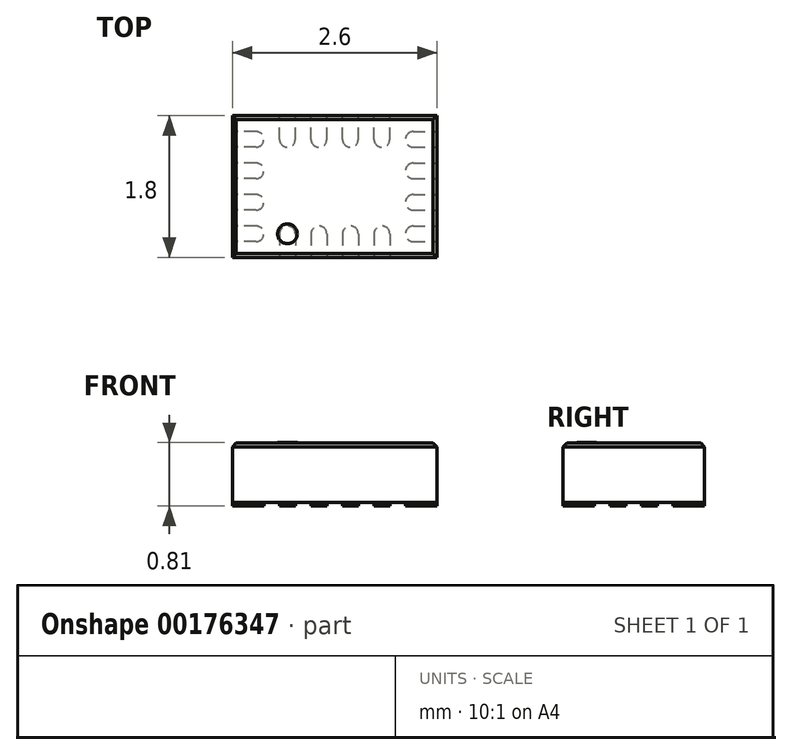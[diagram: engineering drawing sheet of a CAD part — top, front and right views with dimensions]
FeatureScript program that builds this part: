
annotation { "Feature Type Name" : "Feature", "Feature Type Description" : "" }
export const myFeature = defineFeature(function(context is Context, id is Id, definition is map)
    precondition{}
    {
        {
            var Q0;
            Q0=qCreatedBy(makeId("Top.planeOp"),FACE);
            var sketch = newSketch(context, id + "F0", { "sketchPlane" : qUnion([Q0])});
            skLineSegment(sketch, "E0.bottom", {"start": v(1.3, -0.9) * mm, "end": v(-1.3, -0.9) * mm});
            skLineSegment(sketch, "E0.top", {"start": v(1.3, 0.9) * mm, "end": v(-1.3, 0.9) * mm});
            skLineSegment(sketch, "E0.left", {"start": v(1.3, -0.9) * mm, "end": v(1.3, 0.9) * mm});
            skLineSegment(sketch, "E0.right", {"start": v(-1.3, -0.9) * mm, "end": v(-1.3, 0.9) * mm});
            skPoint(sketch, "E0.middle", {"position": v(0, 0) * mm});
            skSolve(sketch);
        }
        {
            var Q0;
            Q0=makeQuery(id+"F0.imprint","IMPRINT",FACE,{"disambiguationData":[TD([[makeQuery(id+"F0.imprint","IMPRINT",EDGE,{"derivedFrom":sQuery(id+"F0.wireOp",EDGE,"E0.bottom")}),-1.0]])]});
            extrude(context, id + "F1", {"entities" : qUnion([Q0]), "depth" : 0.75 * mm});
        }
        {
            var Q0;
            Q0=qCreatedBy(makeId("Top.planeOp"),FACE);
            var sketch = newSketch(context, id + "F2", { "sketchPlane" : qUnion([Q0])});
            skArc(sketch, "E1", {"start": v(-0.5, -0.6) * mm, "mid": v(-0.6, -0.5) * mm, "end": v(-0.7, -0.6) * mm});
            skLineSegment(sketch, "E2", {"start": v(-0.7, -0.6) * mm, "end": v(-0.6, -0.6) * mm, "construction": true});
            skLineSegment(sketch, "E3", {"start": v(-0.5, -0.6) * mm, "end": v(-0.6, -0.6) * mm, "construction": true});
            skLineSegment(sketch, "E4", {"start": v(-0.7, -0.6) * mm, "end": v(-0.7, -0.9) * mm});
            skLineSegment(sketch, "E5", {"start": v(-0.5, -0.6) * mm, "end": v(-0.5, -0.9) * mm});
            skLineSegment(sketch, "E6", {"start": v(-0.5, -0.9) * mm, "end": v(-0.7, -0.9) * mm});
            skLineSegment(sketch, "E7", {"start": v(-0.6, -0.9) * mm, "end": v(-0.6, -0.5) * mm, "construction": true});
            skArc(sketch, "E8.1.0.0", {"start": v(-0.1, -0.6) * mm, "mid": v(-0.2, -0.5) * mm, "end": v(-0.3, -0.6) * mm});
            skLineSegment(sketch, "E8.1.0.1", {"start": v(-0.1, -0.6) * mm, "end": v(-0.1, -0.9) * mm});
            skLineSegment(sketch, "E8.1.0.2", {"start": v(-0.2, -0.9) * mm, "end": v(-0.2, -0.5) * mm, "construction": true});
            skLineSegment(sketch, "E8.1.0.3", {"start": v(-0.3, -0.6) * mm, "end": v(-0.3, -0.9) * mm});
            skLineSegment(sketch, "E8.1.0.4", {"start": v(-0.1, -0.9) * mm, "end": v(-0.3, -0.9) * mm});
            skLineSegment(sketch, "E8.1.0.5", {"start": v(-0.3, -0.6) * mm, "end": v(-0.2, -0.6) * mm, "construction": true});
            skLineSegment(sketch, "E8.1.0.6", {"start": v(-0.1, -0.6) * mm, "end": v(-0.2, -0.6) * mm, "construction": true});
            skArc(sketch, "E8.2.0.0", {"start": v(0.3, -0.6) * mm, "mid": v(0.2, -0.5) * mm, "end": v(0.1, -0.6) * mm});
            skLineSegment(sketch, "E8.2.0.1", {"start": v(0.3, -0.6) * mm, "end": v(0.3, -0.9) * mm});
            skLineSegment(sketch, "E8.2.0.2", {"start": v(0.2, -0.9) * mm, "end": v(0.2, -0.5) * mm, "construction": true});
            skLineSegment(sketch, "E8.2.0.3", {"start": v(0.1, -0.6) * mm, "end": v(0.1, -0.9) * mm});
            skLineSegment(sketch, "E8.2.0.4", {"start": v(0.3, -0.9) * mm, "end": v(0.1, -0.9) * mm});
            skLineSegment(sketch, "E8.2.0.5", {"start": v(0.1, -0.6) * mm, "end": v(0.2, -0.6) * mm, "construction": true});
            skLineSegment(sketch, "E8.2.0.6", {"start": v(0.3, -0.6) * mm, "end": v(0.2, -0.6) * mm, "construction": true});
            skArc(sketch, "E8.3.0.0", {"start": v(0.7, -0.6) * mm, "mid": v(0.6, -0.5) * mm, "end": v(0.5, -0.6) * mm});
            skLineSegment(sketch, "E8.3.0.1", {"start": v(0.7, -0.6) * mm, "end": v(0.7, -0.9) * mm});
            skLineSegment(sketch, "E8.3.0.2", {"start": v(0.6, -0.9) * mm, "end": v(0.6, -0.5) * mm, "construction": true});
            skLineSegment(sketch, "E8.3.0.3", {"start": v(0.5, -0.6) * mm, "end": v(0.5, -0.9) * mm});
            skLineSegment(sketch, "E8.3.0.4", {"start": v(0.7, -0.9) * mm, "end": v(0.5, -0.9) * mm});
            skLineSegment(sketch, "E8.3.0.5", {"start": v(0.5, -0.6) * mm, "end": v(0.6, -0.6) * mm, "construction": true});
            skLineSegment(sketch, "E8.3.0.6", {"start": v(0.7, -0.6) * mm, "end": v(0.6, -0.6) * mm, "construction": true});
            skLineSegment(sketch, "E8.direction1", {"start": v(-0.7, -0.9) * mm, "end": v(-0.3, -0.9) * mm, "construction": true});
            skLineSegment(sketch, "E9", {"start": v(-0.7, -0.75) * mm, "end": v(0.7, -0.75) * mm, "construction": true});
            skLineSegment(sketch, "E10", {"start": v(0, -0.75) * mm, "end": v(0, 0) * mm, "construction": true});
            skArc(sketch, "E11", {"start": v(-1, 0.5) * mm, "mid": v(-0.9, 0.6) * mm, "end": v(-1, 0.7) * mm});
            skLineSegment(sketch, "E12", {"start": v(-1, 0.7) * mm, "end": v(-1, 0.6) * mm, "construction": true});
            skLineSegment(sketch, "E13", {"start": v(-1, 0.5) * mm, "end": v(-1, 0.6) * mm, "construction": true});
            skLineSegment(sketch, "E14", {"start": v(-1, 0.7) * mm, "end": v(-1.3, 0.7) * mm});
            skLineSegment(sketch, "E15", {"start": v(-1, 0.5) * mm, "end": v(-1.3, 0.5) * mm});
            skLineSegment(sketch, "E16", {"start": v(-1.3, 0.5) * mm, "end": v(-1.3, 0.7) * mm});
            skLineSegment(sketch, "E17", {"start": v(-1.3, 0.6) * mm, "end": v(-0.9, 0.6) * mm, "construction": true});
            skArc(sketch, "E18.1.0.0", {"start": v(-1, 0.1) * mm, "mid": v(-0.9, 0.2) * mm, "end": v(-1, 0.3) * mm});
            skLineSegment(sketch, "E18.1.0.1", {"start": v(-1, 0.1) * mm, "end": v(-1.3, 0.1) * mm});
            skLineSegment(sketch, "E18.1.0.2", {"start": v(-1.3, 0.2) * mm, "end": v(-0.9, 0.2) * mm, "construction": true});
            skLineSegment(sketch, "E18.1.0.3", {"start": v(-1, 0.3) * mm, "end": v(-1.3, 0.3) * mm});
            skLineSegment(sketch, "E18.1.0.4", {"start": v(-1.3, 0.1) * mm, "end": v(-1.3, 0.3) * mm});
            skLineSegment(sketch, "E18.1.0.5", {"start": v(-1, 0.3) * mm, "end": v(-1, 0.2) * mm, "construction": true});
            skLineSegment(sketch, "E18.direction1", {"start": v(-1.3, 0.7) * mm, "end": v(-1.3, 0.3) * mm, "construction": true});
            skLineSegment(sketch, "E19", {"start": v(-1.15, 0.7) * mm, "end": v(-1.15, 0) * mm, "construction": true});
            skLineSegment(sketch, "E20", {"start": v(-1.15, 0) * mm, "end": v(0, 0) * mm, "construction": true});
            skLineSegment(sketch, "E21.MirrorCS", {"start": v(1.3, 0.7) * mm, "end": v(1.3, 0.3) * mm, "construction": true});
            skLineSegment(sketch, "E22.MirrorCS", {"start": v(1.3, 0.1) * mm, "end": v(1.3, 0.3) * mm});
            skLineSegment(sketch, "E23.MirrorCS", {"start": v(1.3, 0.6) * mm, "end": v(0.9, 0.6) * mm, "construction": true});
            skLineSegment(sketch, "E24.MirrorCS", {"start": v(1, 0.7) * mm, "end": v(1.3, 0.7) * mm});
            skArc(sketch, "E25.MirrorCS", {"start": v(1, 0.5) * mm, "mid": v(0.9, 0.6) * mm, "end": v(1, 0.7) * mm});
            skLineSegment(sketch, "E26.MirrorCS", {"start": v(1, 0.3) * mm, "end": v(1.3, 0.3) * mm});
            skLineSegment(sketch, "E27.MirrorCS", {"start": v(1, 0.5) * mm, "end": v(1, 0.6) * mm, "construction": true});
            skLineSegment(sketch, "E28.MirrorCS", {"start": v(1, 0.5) * mm, "end": v(1.3, 0.5) * mm});
            skArc(sketch, "E29.MirrorCS", {"start": v(1, 0.1) * mm, "mid": v(0.9, 0.2) * mm, "end": v(1, 0.3) * mm});
            skLineSegment(sketch, "E30.MirrorCS", {"start": v(1, 0.1) * mm, "end": v(1.3, 0.1) * mm});
            skLineSegment(sketch, "E31.MirrorCS", {"start": v(1.3, 0.5) * mm, "end": v(1.3, 0.7) * mm});
            skLineSegment(sketch, "E32.MirrorCS", {"start": v(-1, 0.5) * mm, "end": v(-1, 0.7) * mm, "construction": true});
            skSolve(sketch);
        }
        {
            var Q0;
            Q0 = qSketchRegion(id + "F2", true);
            extrude(context, id + "F3", {"entities" : qUnion([Q0]), "oppositeDirection" : true, "depth" : 0.05 * mm});
        }
        {
            var Q0;
            Q0=makeQuery(id+"F3.opExtrude","SWEPT_BODY",BODY,{"disambiguationData":[OSD([sQuery(id+"F2.wireOp",EDGE,"E8.3.0.0"),sQuery(id+"F2.wireOp",EDGE,"E8.3.0.1"),sQuery(id+"F2.wireOp",EDGE,"E8.3.0.3"),sQuery(id+"F2.wireOp",EDGE,"E8.3.0.4")])]});
            var Q1;
            Q1=makeQuery(id+"F3.opExtrude","SWEPT_BODY",BODY,{"disambiguationData":[OSD([sQuery(id+"F2.wireOp",EDGE,"E8.2.0.0"),sQuery(id+"F2.wireOp",EDGE,"E8.2.0.1"),sQuery(id+"F2.wireOp",EDGE,"E8.2.0.3"),sQuery(id+"F2.wireOp",EDGE,"E8.2.0.4")])]});
            var Q2;
            Q2=makeQuery(id+"F3.opExtrude","SWEPT_BODY",BODY,{"disambiguationData":[OSD([sQuery(id+"F2.wireOp",EDGE,"E8.1.0.0"),sQuery(id+"F2.wireOp",EDGE,"E8.1.0.1"),sQuery(id+"F2.wireOp",EDGE,"E8.1.0.3"),sQuery(id+"F2.wireOp",EDGE,"E8.1.0.4")])]});
            var Q3;
            Q3=makeQuery(id+"F3.opExtrude","SWEPT_BODY",BODY,{"disambiguationData":[OSD([sQuery(id+"F2.wireOp",EDGE,"E1"),sQuery(id+"F2.wireOp",EDGE,"E4"),sQuery(id+"F2.wireOp",EDGE,"E5"),sQuery(id+"F2.wireOp",EDGE,"E6")])]});
            var Q4;
            Q4=makeQuery(id+"F3.opExtrude","SWEPT_BODY",BODY,{"disambiguationData":[OSD([sQuery(id+"F2.wireOp",EDGE,"E22.MirrorCS"),sQuery(id+"F2.wireOp",EDGE,"E26.MirrorCS"),sQuery(id+"F2.wireOp",EDGE,"E29.MirrorCS"),sQuery(id+"F2.wireOp",EDGE,"E30.MirrorCS")])]});
            var Q5;
            Q5=makeQuery(id+"F3.opExtrude","SWEPT_BODY",BODY,{"disambiguationData":[OSD([sQuery(id+"F2.wireOp",EDGE,"E24.MirrorCS"),sQuery(id+"F2.wireOp",EDGE,"E25.MirrorCS"),sQuery(id+"F2.wireOp",EDGE,"E28.MirrorCS"),sQuery(id+"F2.wireOp",EDGE,"E31.MirrorCS")])]});
            var Q6;
            Q6=makeQuery(id+"F3.opExtrude","SWEPT_BODY",BODY,{"disambiguationData":[OSD([sQuery(id+"F2.wireOp",EDGE,"E11"),sQuery(id+"F2.wireOp",EDGE,"E14"),sQuery(id+"F2.wireOp",EDGE,"E15"),sQuery(id+"F2.wireOp",EDGE,"E16")])]});
            var Q7;
            Q7=makeQuery(id+"F3.opExtrude","SWEPT_BODY",BODY,{"disambiguationData":[OSD([sQuery(id+"F2.wireOp",EDGE,"E18.1.0.0"),sQuery(id+"F2.wireOp",EDGE,"E18.1.0.1"),sQuery(id+"F2.wireOp",EDGE,"E18.1.0.3"),sQuery(id+"F2.wireOp",EDGE,"E18.1.0.4")])]});
            var Q8;
            Q8=qCreatedBy(makeId("Front.planeOp"),FACE);
            mirror(context, id + "F4", {"entities" : qUnion([Q0, Q1, Q2, Q3, Q4, Q5, Q6, Q7]), "mirrorPlane" : qUnion([Q8])});
        }
        {
            var Q0;
            Q0=makeQuery(id+"F1.opExtrude","CAP_FACE",FACE,{"disambiguationData":[OSD([sQuery(id+"F0.wireOp",EDGE,"E0.bottom"),sQuery(id+"F0.wireOp",EDGE,"E0.top"),sQuery(id+"F0.wireOp",EDGE,"E0.left"),sQuery(id+"F0.wireOp",EDGE,"E0.right")])],"isStart":false});
            var sketch = newSketch(context, id + "F5", { "sketchPlane" : qUnion([Q0])});
            skCircle(sketch, "E33", {"center": v(-0.6, -0.6) * mm, "radius": 0.12 * mm});
            skSolve(sketch);
        }
        {
            var Q0;
            Q0=makeQuery(id+"F5.imprint","IMPRINT",FACE,{"disambiguationData":[TD([[makeQuery(id+"F5.imprint","IMPRINT",EDGE,{"derivedFrom":sQuery(id+"F5.wireOp",EDGE,"E33")}),1.0]])]});
            extrude(context, id + "F6", {"entities" : qUnion([Q0]), "depth" : 0.01 * mm});
        }
        {
            var Q0;
            Q0=makeQuery(id+"F1.opExtrude","CAP_FACE",FACE,{"disambiguationData":[OSD([sQuery(id+"F0.wireOp",EDGE,"E0.bottom"),sQuery(id+"F0.wireOp",EDGE,"E0.top"),sQuery(id+"F0.wireOp",EDGE,"E0.left"),sQuery(id+"F0.wireOp",EDGE,"E0.right")])],"isStart":false});
            chamfer(context, id + "F7", {"entities" : qUnion([Q0]), "width" : 0.05 * mm, "tangentPropagation" : true});
        }
    });
